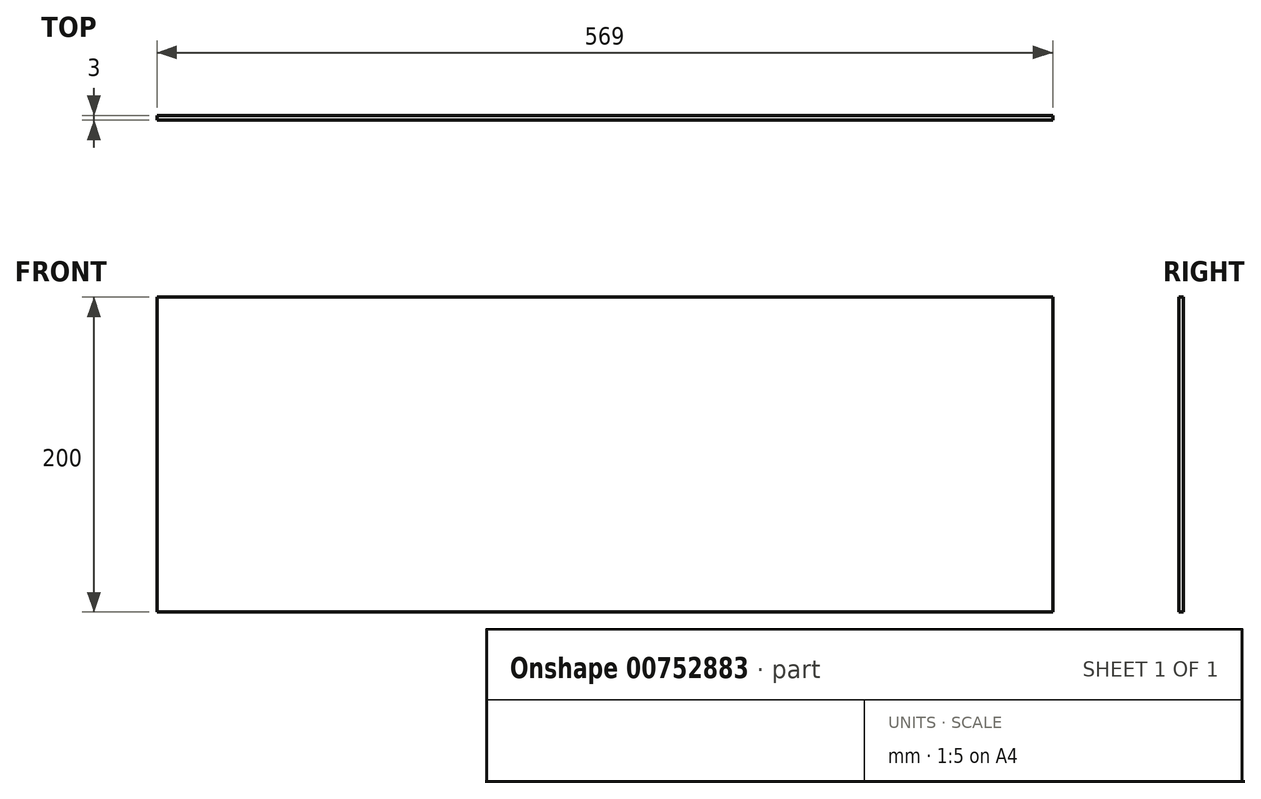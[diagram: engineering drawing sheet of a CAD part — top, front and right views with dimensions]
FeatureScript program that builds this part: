
annotation { "Feature Type Name" : "Feature", "Feature Type Description" : "" }
export const myFeature = defineFeature(function(context is Context, id is Id, definition is map)
    precondition{}
    {
        {
            var Q0;
            Q0=qCreatedBy(makeId("Front.planeOp"),FACE);
            var sketch = newSketch(context, id + "F0", { "sketchPlane" : qUnion([Q0])});
            skLineSegment(sketch, "E0.bottom", {"start": v(-284.5, 100) * mm, "end": v(284.5, 100) * mm});
            skLineSegment(sketch, "E0.top", {"start": v(-284.5, -100) * mm, "end": v(284.5, -100) * mm});
            skLineSegment(sketch, "E0.left", {"start": v(-284.5, 100) * mm, "end": v(-284.5, -100) * mm});
            skLineSegment(sketch, "E0.right", {"start": v(284.5, 100) * mm, "end": v(284.5, -100) * mm});
            skPoint(sketch, "E0.middle", {"position": v(0, 0) * mm});
            skSolve(sketch);
        }
        {
            var Q0;
            Q0=makeQuery(id+"F0.imprint","IMPRINT",FACE,{"disambiguationData":[TD([[makeQuery(id+"F0.imprint","IMPRINT",EDGE,{"derivedFrom":sQuery(id+"F0.wireOp",EDGE,"E0.bottom")}),-1.0]])]});
            extrude(context, id + "F1", {"entities" : qUnion([Q0]), "depth" : 3 * mm, "offsetDistance" : 25 * mm});
        }
    });
